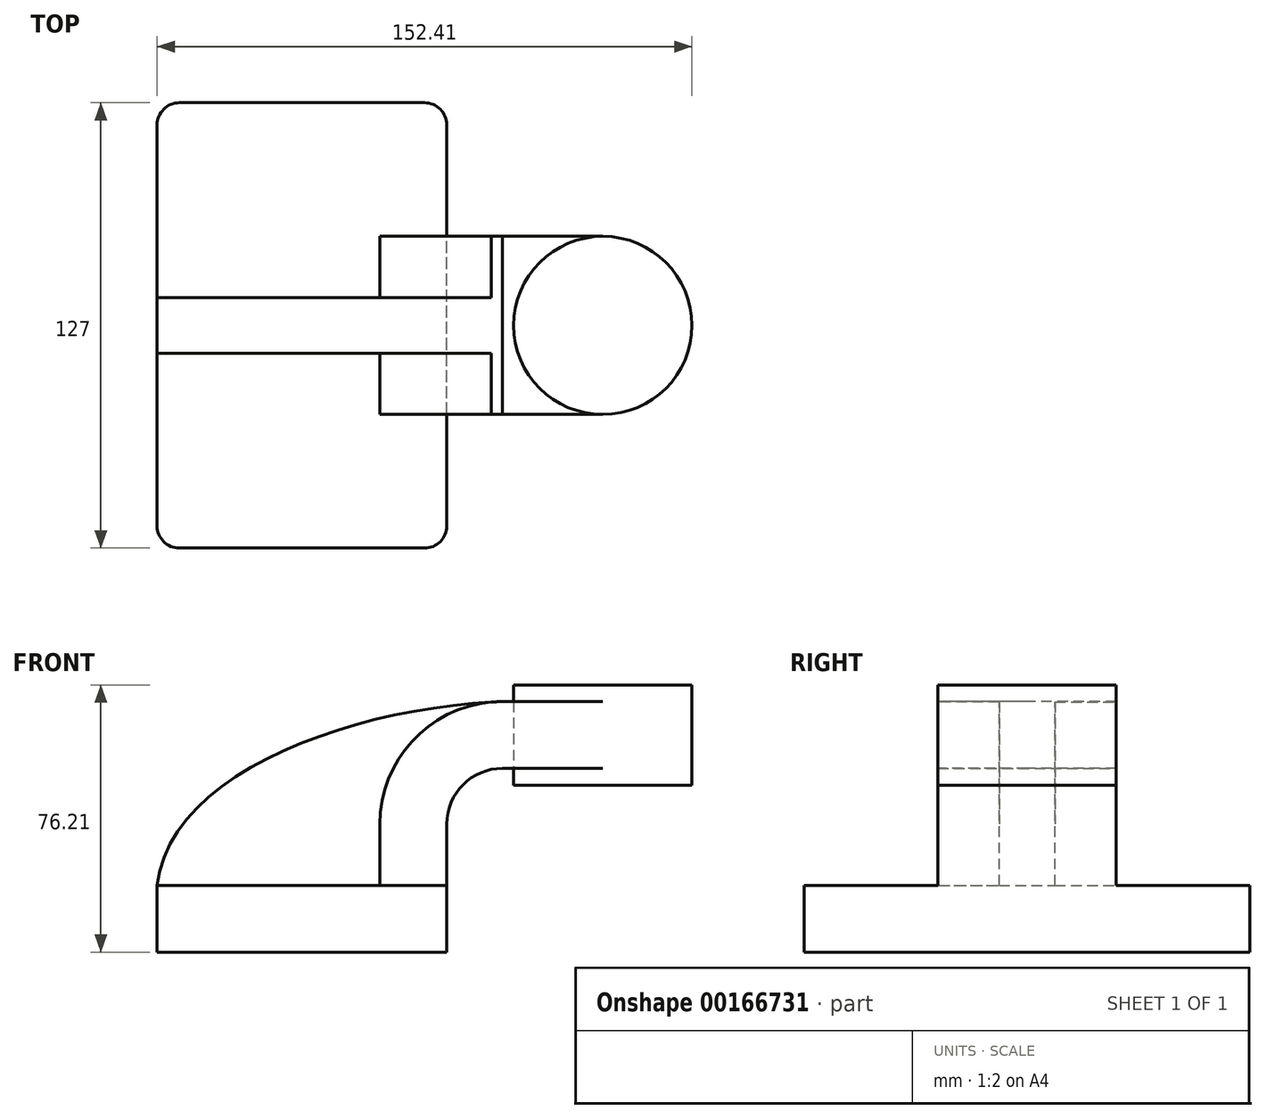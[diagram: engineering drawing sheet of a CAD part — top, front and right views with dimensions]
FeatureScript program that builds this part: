
annotation { "Feature Type Name" : "Feature", "Feature Type Description" : "" }
export const myFeature = defineFeature(function(context is Context, id is Id, definition is map)
    precondition{}
    {
        {
            var Q0;
            Q0=qCreatedBy(makeId("Front.planeOp"),FACE);
            var sketch = newSketch(context, id + "F0", { "sketchPlane" : qUnion([Q0])});
            skLineSegment(sketch, "E0.bottom", {"start": v(41.28, -9.52) * mm, "end": v(-41.28, -9.53) * mm});
            skLineSegment(sketch, "E0.top", {"start": v(41.28, 9.53) * mm, "end": v(-41.28, 9.53) * mm});
            skLineSegment(sketch, "E0.left", {"start": v(41.28, -9.52) * mm, "end": v(41.28, 9.53) * mm});
            skLineSegment(sketch, "E0.right", {"start": v(-41.28, -9.53) * mm, "end": v(-41.28, 9.53) * mm});
            skPoint(sketch, "E0.middle", {"position": v(0, 0) * mm});
            skLineSegment(sketch, "E1.bottom", {"start": v(111.12, 38.1) * mm, "end": v(60.32, 38.1) * mm});
            skLineSegment(sketch, "E1.top", {"start": v(111.12, 66.68) * mm, "end": v(60.32, 66.68) * mm});
            skLineSegment(sketch, "E1.left", {"start": v(111.12, 38.1) * mm, "end": v(111.12, 66.68) * mm});
            skLineSegment(sketch, "E1.right", {"start": v(60.32, 38.1) * mm, "end": v(60.32, 66.67) * mm});
            skPoint(sketch, "E1.middle", {"position": v(85.72, 52.39) * mm});
            skLineSegment(sketch, "E2", {"start": v(41.28, 9.53) * mm, "end": v(41.28, 27) * mm});
            skArc(sketch, "E3", {"start": v(41.27, 27) * mm, "mid": v(45.92, 38.23) * mm, "end": v(57.15, 42.88) * mm});
            skLineSegment(sketch, "E4", {"start": v(57.15, 42.88) * mm, "end": v(85.72, 42.88) * mm});
            skLineSegment(sketch, "E5.0", {"start": v(57.15, 61.93) * mm, "end": v(85.72, 61.93) * mm});
            skArc(sketch, "E5.1", {"start": v(22.23, 27) * mm, "mid": v(32.45, 51.7) * mm, "end": v(57.15, 61.93) * mm});
            skLineSegment(sketch, "E5.2", {"start": v(22.22, 9.53) * mm, "end": v(22.22, 27) * mm});
            skLineSegment(sketch, "E6", {"start": v(85.72, 38.1) * mm, "end": v(85.72, 66.68) * mm});
            skFitSpline(sketch, "E7", {"points": [v(-41.28, 9.52) * mm, v(57.15, 61.93) * mm], "startDerivative": vector(10.88, 97.75) * mm, "endDerivative": vector(124.87, 4.47) * mm});
            skSolve(sketch);
        }
        {
            var Q0;
            Q0=makeQuery(id+"F0.imprint","IMPRINT",FACE,{"disambiguationData":[TD([[makeQuery(id+"F0.imprint","IMPRINT",EDGE,{"derivedFrom":sQuery(id+"F0.wireOp",EDGE,"E0.bottom")}),-1.0]])]});
            extrude(context, id + "F1", {"entities" : qUnion([Q0]), "endBound" : BoundingType.SYMMETRIC, "depth" : 127 * mm});
        }
        {
            var Q0;
            {var subQ1=sQuery(id+"F0.wireOp",EDGE,"E2");Q0=makeQuery(id+"F0.imprint","IMPRINT",FACE,{"disambiguationData":[TD([[makeQuery(id+"F0.imprint","IMPRINT",EDGE,{"derivedFrom":subQ1}),1.0]])]});}
            var Q1;
            {var subQ0=sQuery(id+"F0.wireOp",EDGE,"E4");var subQ1=sQuery(id+"F0.wireOp",EDGE,"E1.right");var subQ2=makeQuery(id+"F0.imprint","INTERSECT",VERTEX,{"derivedFrom":[subQ1,subQ0]});Q1=makeQuery(id+"F0.imprint","IMPRINT",FACE,{"disambiguationData":[TD([[makeQuery(id+"F0.imprint","IMPRINT",EDGE,{"disambiguationData":[TD([[subQ2,-1.0]])],"derivedFrom":subQ1}),-1.0]])]});}
            extrude(context, id + "F2", {"entities" : qUnion([Q0, Q1]), "operationType" : NewBodyOperationType.ADD, "endBound" : BoundingType.SYMMETRIC, "depth" : 50.8 * mm});
        }
        {
            var Q0;
            {var subQ3=sQuery(id+"F0.wireOp",EDGE,"E5.2");Q0=makeQuery(id+"F0.imprint","IMPRINT",FACE,{"disambiguationData":[TD([[makeQuery(id+"F0.imprint","IMPRINT",EDGE,{"derivedFrom":subQ3}),1.0]])]});}
            extrude(context, id + "F3", {"entities" : qUnion([Q0]), "operationType" : NewBodyOperationType.ADD, "endBound" : BoundingType.SYMMETRIC, "depth" : 15.88 * mm});
        }
        {
            var Q0;
            {var subQ0=sQuery(id+"F0.wireOp",EDGE,"E1.left");Q0=makeQuery(id+"F0.imprint","IMPRINT",FACE,{"disambiguationData":[TD([[makeQuery(id+"F0.imprint","IMPRINT",EDGE,{"derivedFrom":subQ0}),1.0]])]});}
            var Q1;
            Q1=sQuery(id+"F0.wireOp",EDGE,"E6");
            revolve(context, id + "F4", {"entities" : qUnion([Q0]), "axis" : qUnion([Q1]), "revolveType" : RevolveType.FULL});
        }
        {
            var Q0;
            Q0=makeQuery(id+"F1.opExtrude","CAP_EDGE",EDGE,{"disambiguationData":[OSD([sQuery(id+"F0.wireOp",EDGE,"E0.left")])],"isStart":false});
            var Q1;
            Q1=makeQuery(id+"F1.opExtrude","CAP_EDGE",EDGE,{"disambiguationData":[OSD([sQuery(id+"F0.wireOp",EDGE,"E0.right")])],"isStart":false});
            var Q2;
            Q2=makeQuery(id+"F1.opExtrude","CAP_EDGE",EDGE,{"disambiguationData":[OSD([sQuery(id+"F0.wireOp",EDGE,"E0.left")])],"isStart":true});
            var Q3;
            Q3=makeQuery(id+"F1.opExtrude","CAP_EDGE",EDGE,{"disambiguationData":[OSD([sQuery(id+"F0.wireOp",EDGE,"E0.right")])],"isStart":true});
            fillet(context, id + "F5", {"entities" : qUnion([Q0, Q1, Q2, Q3]), "radius" : 6.35 * mm, "tangentPropagation" : true, "allowEdgeOverflow" : false});
        }
    });
